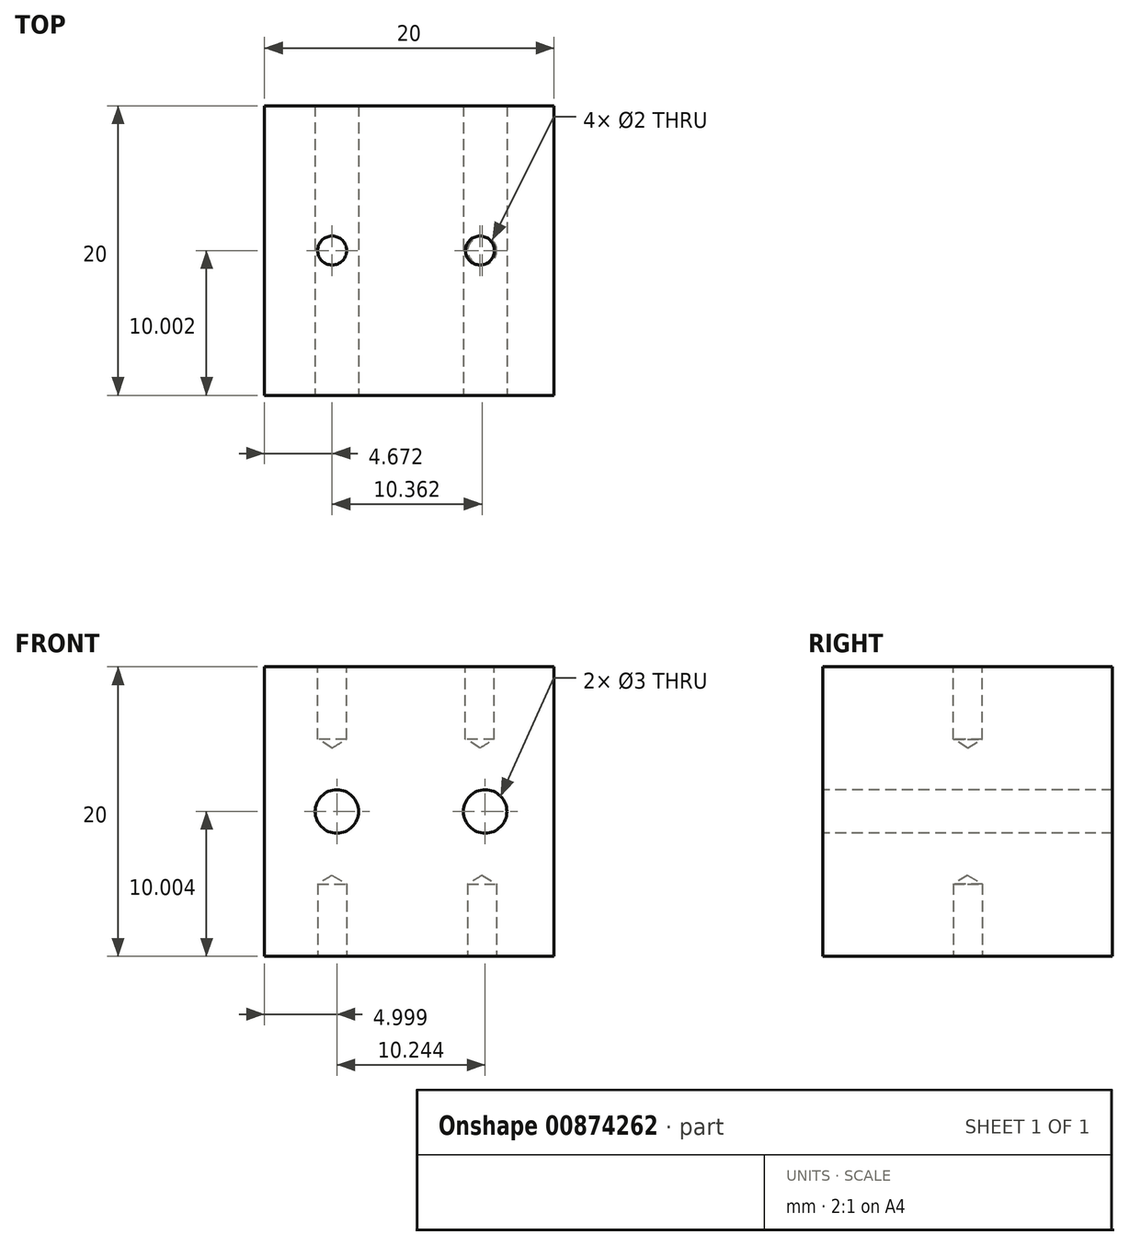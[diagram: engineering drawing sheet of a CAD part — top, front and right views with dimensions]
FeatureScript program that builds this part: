
annotation { "Feature Type Name" : "Feature", "Feature Type Description" : "" }
export const myFeature = defineFeature(function(context is Context, id is Id, definition is map)
    precondition{}
    {
        {
            var Q0;
            Q0=qCreatedBy(makeId("Top.planeOp"),FACE);
            var sketch = newSketch(context, id + "F0", { "sketchPlane" : qUnion([Q0])});
            skLineSegment(sketch, "E0.bottom", {"start": v(-17.55, 17.9) * mm, "end": v(2.45, 17.9) * mm});
            skLineSegment(sketch, "E0.top", {"start": v(-17.55, -2.1) * mm, "end": v(2.45, -2.1) * mm});
            skLineSegment(sketch, "E0.left", {"start": v(-17.55, 17.9) * mm, "end": v(-17.55, -2.1) * mm});
            skLineSegment(sketch, "E0.right", {"start": v(2.45, 17.9) * mm, "end": v(2.45, -2.1) * mm});
            skPoint(sketch, "E1", {"position": v(-12.88, 7.9) * mm});
            skPoint(sketch, "E2", {"position": v(-2.52, 7.9) * mm});
            skPoint(sketch, "E3.start.orphan", {"position": v(-17.55, 7.9) * mm});
            skPoint(sketch, "E4.trimOffspring.end.orphan", {"position": v(2.45, 7.9) * mm});
            skSolve(sketch);
        }
        {
            var Q0;
            Q0 = qSketchRegion(id + "F0", true);
            extrude(context, id + "F1", {"entities" : qUnion([Q0]), "depth" : 20 * mm, "offsetDistance" : 25 * mm});
        }
        {
            var Q0;
            Q0 = qSketchRegion(id + "F0", true);
            extrude(context, id + "F2", {"entities" : qUnion([Q0]), "operationType" : NewBodyOperationType.ADD, "depth" : 20 * mm, "offsetDistance" : 25 * mm});
        }
        {
            var Q0;
            Q0=sQuery(id+"F0.wireOp",VERTEX,"E1");
            var Q1;
            Q1=sQuery(id+"F0.wireOp",VERTEX,"E2");
            var Q2;
            Q2=makeQuery(id+"F1.opExtrude","SWEPT_BODY",BODY,{"disambiguationData":[OSD([sQuery(id+"F0.wireOp",EDGE,"E0.bottom"),sQuery(id+"F0.wireOp",EDGE,"E0.top"),sQuery(id+"F0.wireOp",EDGE,"E0.left"),sQuery(id+"F0.wireOp",EDGE,"E0.right")])]});
            hole(context, id + "F3", {"style" : HoleStyle.SIMPLE, "endStyle" : HoleEndStyle.BLIND, "oppositeDirection" : true, "holeDiameter" : 2 * mm, "majorDiameter" : 5 * mm, "holeDepth" : 5 * mm, "isTappedThrough" : true, "tappedDepth" : 12 * mm, "tapClearance" : 3, "locations" : qUnion([Q0, Q1]), "scope" : qUnion([Q2])});
        }
        {
            var Q0;
            Q0=makeQuery(id+"F1.opExtrude","CAP_FACE",FACE,{"disambiguationData":[OSD([sQuery(id+"F0.wireOp",EDGE,"E0.bottom"),sQuery(id+"F0.wireOp",EDGE,"E0.top"),sQuery(id+"F0.wireOp",EDGE,"E0.left"),sQuery(id+"F0.wireOp",EDGE,"E0.right")])],"isStart":false});
            var sketch = newSketch(context, id + "F4", { "sketchPlane" : qUnion([Q0])});
            skPoint(sketch, "E5", {"position": v(-12.88, 7.9) * mm});
            skPoint(sketch, "E5.positionSnap0", {"position": v(2.45, 7.9) * mm});
            skPoint(sketch, "E6", {"position": v(-2.67, 7.9) * mm});
            skSolve(sketch);
        }
        {
            var Q0;
            Q0=sQuery(id+"F4.wireOp",VERTEX,"E5");
            var Q1;
            Q1=sQuery(id+"F4.wireOp",VERTEX,"E6");
            var Q2;
            Q2=makeQuery(id+"F1.opExtrude","SWEPT_BODY",BODY,{"disambiguationData":[OSD([sQuery(id+"F0.wireOp",EDGE,"E0.bottom"),sQuery(id+"F0.wireOp",EDGE,"E0.top"),sQuery(id+"F0.wireOp",EDGE,"E0.left"),sQuery(id+"F0.wireOp",EDGE,"E0.right")])]});
            hole(context, id + "F5", {"style" : HoleStyle.SIMPLE, "endStyle" : HoleEndStyle.BLIND, "holeDiameter" : 2 * mm, "majorDiameter" : 5 * mm, "holeDepth" : 5 * mm, "isTappedThrough" : true, "tappedDepth" : 12 * mm, "tapClearance" : 3, "locations" : qUnion([Q0, Q1]), "scope" : qUnion([Q2])});
        }
        {
            var Q0;
            Q0=makeQuery(id+"F1.opExtrude","SWEPT_FACE",FACE,{"disambiguationData":[OSD([sQuery(id+"F0.wireOp",EDGE,"E0.top")])]});
            var sketch = newSketch(context, id + "F6", { "sketchPlane" : qUnion([Q0])});
            skLineSegment(sketch, "E7", {"start": v(-17.55, 20) * mm, "end": v(2.45, 0) * mm});
            skLineSegment(sketch, "E8", {"start": v(2.45, 0) * mm, "end": v(-17.55, 0) * mm});
            skLineSegment(sketch, "E9", {"start": v(-17.55, 0) * mm, "end": v(2.34, 19.9) * mm});
            skLineSegment(sketch, "E10", {"start": v(-7.55, 10) * mm, "end": v(-17.55, 10) * mm});
            skLineSegment(sketch, "E11", {"start": v(-17.55, 10) * mm, "end": v(2.45, 10) * mm});
            skCircle(sketch, "E12", {"center": v(-7.55, 10) * mm, "radius": 5.25 * mm});
            skPoint(sketch, "E13", {"position": v(-12.55, 10) * mm});
            skPoint(sketch, "E14", {"position": v(-2.3, 10) * mm});
            skSolve(sketch);
        }
        {
            var Q0;
            Q0=sQuery(id+"F6.wireOp",VERTEX,"E13");
            var Q1;
            Q1=sQuery(id+"F6.wireOp",VERTEX,"E14");
            var Q2;
            Q2=makeQuery(id+"F1.opExtrude","SWEPT_BODY",BODY,{"disambiguationData":[OSD([sQuery(id+"F0.wireOp",EDGE,"E0.bottom"),sQuery(id+"F0.wireOp",EDGE,"E0.top"),sQuery(id+"F0.wireOp",EDGE,"E0.left"),sQuery(id+"F0.wireOp",EDGE,"E0.right")])]});
            hole(context, id + "F7", {"style" : HoleStyle.SIMPLE, "endStyle" : HoleEndStyle.THROUGH, "holeDiameter" : 3 * mm, "majorDiameter" : 5 * mm, "isTappedThrough" : true, "tappedDepth" : 12 * mm, "tapClearance" : 3, "locations" : qUnion([Q0, Q1]), "scope" : qUnion([Q2])});
        }
    });
